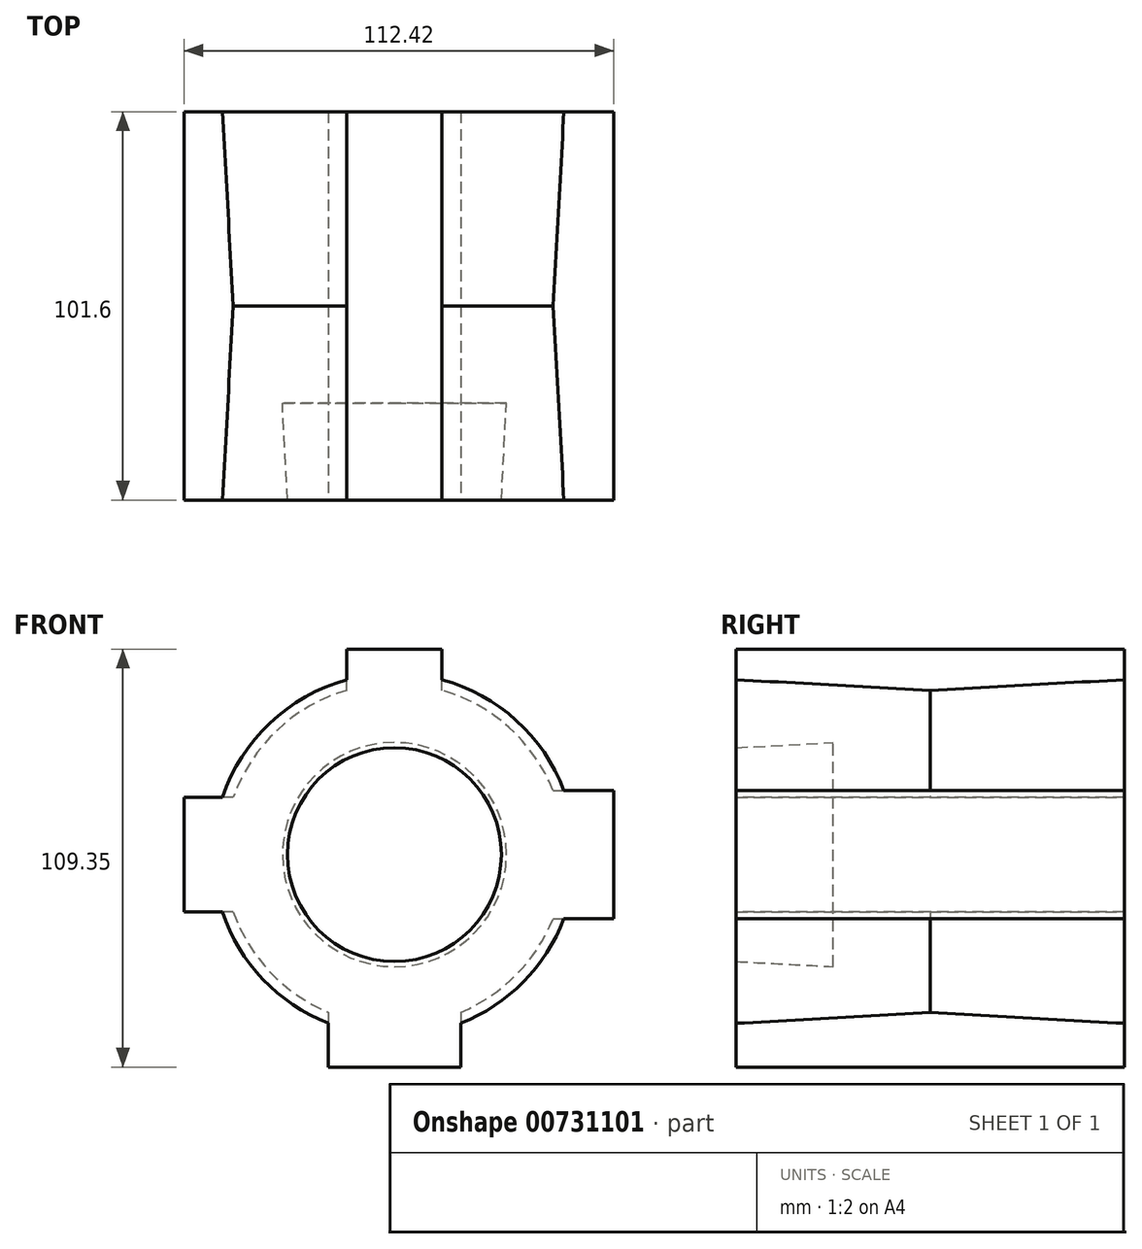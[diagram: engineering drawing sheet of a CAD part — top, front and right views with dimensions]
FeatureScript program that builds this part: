
annotation { "Feature Type Name" : "Feature", "Feature Type Description" : "" }
export const myFeature = defineFeature(function(context is Context, id is Id, definition is map)
    precondition{}
    {
        {
            var Q0;
            Q0=qCreatedBy(makeId("Front.planeOp"),FACE);
            var sketch = newSketch(context, id + "F0", { "sketchPlane" : qUnion([Q0])});
            skCircle(sketch, "E0", {"center": v(0, 0) * mm, "radius": 44.75 * mm});
            skSolve(sketch);
        }
        {
            var Q0;
            Q0=makeQuery(id+"F0.imprint","IMPRINT",FACE,{"disambiguationData":[TD([[makeQuery(id+"F0.imprint","IMPRINT",EDGE,{"derivedFrom":sQuery(id+"F0.wireOp",EDGE,"E0")}),1.0]])]});
            extrude(context, id + "F1", {"entities" : qUnion([Q0]), "endBound" : BoundingType.SYMMETRIC, "depth" : 101.6 * mm, "offsetDistance" : 25.4 * mm, "hasDraft" : true, "draftAngle" : 3 * degree});
        }
        {
            var Q0;
            Q0=makeQuery(id+"F1.opExtrude","CAP_FACE",FACE,{"disambiguationData":[OSD([sQuery(id+"F0.wireOp",EDGE,"E0")])],"isStart":true});
            var sketch = newSketch(context, id + "F2", { "sketchPlane" : qUnion([Q0])});
            skLineSegment(sketch, "E1.bottom", {"start": v(12.45, 53.77) * mm, "end": v(-12.45, 53.77) * mm});
            skLineSegment(sketch, "E1.top", {"start": v(12.45, 26.34) * mm, "end": v(-12.45, 26.34) * mm});
            skLineSegment(sketch, "E1.left", {"start": v(12.45, 53.77) * mm, "end": v(12.45, 26.34) * mm});
            skLineSegment(sketch, "E1.right", {"start": v(-12.45, 53.77) * mm, "end": v(-12.45, 26.34) * mm});
            skPoint(sketch, "E1.middle", {"position": v(0, 40.06) * mm});
            skLineSegment(sketch, "E2.bottom", {"start": v(55.04, 14.98) * mm, "end": v(17.86, 14.98) * mm});
            skLineSegment(sketch, "E2.top", {"start": v(55.04, -14.98) * mm, "end": v(17.86, -14.98) * mm});
            skLineSegment(sketch, "E2.left", {"start": v(55.04, 14.98) * mm, "end": v(55.04, -14.98) * mm});
            skLineSegment(sketch, "E2.right", {"start": v(17.86, 14.98) * mm, "end": v(17.86, -14.98) * mm});
            skPoint(sketch, "E2.middle", {"position": v(36.45, 0) * mm});
            skLineSegment(sketch, "E3.bottom", {"start": v(17.32, -55.58) * mm, "end": v(-17.32, -55.58) * mm});
            skLineSegment(sketch, "E3.top", {"start": v(17.32, -14.8) * mm, "end": v(-17.32, -14.8) * mm});
            skLineSegment(sketch, "E3.left", {"start": v(17.32, -55.58) * mm, "end": v(17.32, -14.8) * mm});
            skLineSegment(sketch, "E3.right", {"start": v(-17.32, -55.58) * mm, "end": v(-17.32, -14.8) * mm});
            skPoint(sketch, "E3.middle", {"position": v(0, -35.19) * mm});
            skLineSegment(sketch, "E4.bottom", {"start": v(-57.38, -16.78) * mm, "end": v(-5.77, -16.78) * mm});
            skLineSegment(sketch, "E4.top", {"start": v(-57.38, 16.78) * mm, "end": v(-5.77, 16.78) * mm});
            skLineSegment(sketch, "E4.left", {"start": v(-57.38, -16.78) * mm, "end": v(-57.38, 16.78) * mm});
            skLineSegment(sketch, "E4.right", {"start": v(-5.77, -16.78) * mm, "end": v(-5.77, 16.78) * mm});
            skPoint(sketch, "E4.middle", {"position": v(-31.58, 0) * mm});
            skSolve(sketch);
        }
        {
            var Q0;
            {var subQ0=sQuery(id+"F2.wireOp",EDGE,"E2.right");Q0=makeQuery(id+"F2.imprint","IMPRINT",FACE,{"disambiguationData":[TD([[makeQuery(id+"F2.imprint","IMPRINT",EDGE,{"derivedFrom":subQ0}),1.0]])]});}
            var Q1;
            Q1 = qSketchRegion(id + "F2", true);
            extrude(context, id + "F3", {"entities" : qUnion([Q0, Q1]), "operationType" : NewBodyOperationType.ADD, "oppositeDirection" : true, "depth" : 101.6 * mm, "offsetDistance" : 25.4 * mm});
        }
        {
            var Q0;
            Q0=makeQuery(id+"F3.boolean.opBoolean","MERGE",FACE,{"derivedFrom":[makeQuery(id+"F1.opExtrude","CAP_FACE",FACE,{"disambiguationData":[OSD([sQuery(id+"F0.wireOp",EDGE,"E0")])],"isStart":false}),makeQuery(id+"F3.opExtrude","CAP_FACE",FACE,{"disambiguationData":[OSD([sQuery(id+"F2.wireOp",EDGE,"E1.bottom"),sQuery(id+"F2.wireOp",EDGE,"E1.top"),sQuery(id+"F2.wireOp",EDGE,"E1.left"),sQuery(id+"F2.wireOp",EDGE,"E1.right")])],"isStart":false}),makeQuery(id+"F3.opExtrude","CAP_FACE",FACE,{"disambiguationData":[OSD([sQuery(id+"F2.wireOp",EDGE,"E2.bottom"),sQuery(id+"F2.wireOp",EDGE,"E2.top"),sQuery(id+"F2.wireOp",EDGE,"E2.left"),sQuery(id+"F2.wireOp",EDGE,"E2.right")])],"isStart":false}),makeQuery(id+"F3.opExtrude","CAP_FACE",FACE,{"disambiguationData":[OSD([sQuery(id+"F2.wireOp",EDGE,"E3.bottom"),sQuery(id+"F2.wireOp",EDGE,"E3.top"),sQuery(id+"F2.wireOp",EDGE,"E3.left"),sQuery(id+"F2.wireOp",EDGE,"E3.right"),sQuery(id+"F2.wireOp",EDGE,"E4.bottom"),sQuery(id+"F2.wireOp",EDGE,"E4.top"),sQuery(id+"F2.wireOp",EDGE,"E4.left"),sQuery(id+"F2.wireOp",EDGE,"E4.right")])],"isStart":false})]});
            var sketch = newSketch(context, id + "F4", { "sketchPlane" : qUnion([Q0])});
            skCircle(sketch, "E5", {"center": v(0, 0) * mm, "radius": 27.98 * mm});
            skSolve(sketch);
        }
        {
            var Q0;
            Q0 = qSketchRegion(id + "F4", true);
            extrude(context, id + "F5", {"entities" : qUnion([Q0]), "operationType" : NewBodyOperationType.REMOVE, "oppositeDirection" : true, "depth" : 25.4 * mm, "offsetDistance" : 25.4 * mm, "hasDraft" : true, "draftAngle" : 3 * degree});
        }
    });
